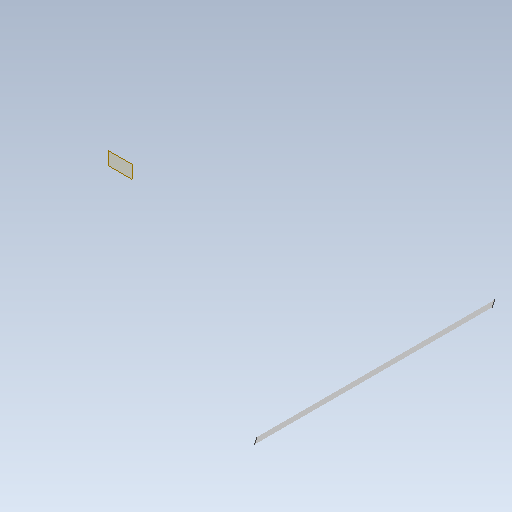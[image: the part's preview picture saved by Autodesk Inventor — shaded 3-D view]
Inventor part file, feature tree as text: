
AUTODESK INVENTOR PART (.ipt)
format: ipt  version: 2021 (Build 250183000, 183)  size: 104,960 bytes
history: native  units: mm
features: other x4, extrude x1, chamfer x1, reference x1
ambient origin geometry x8: Origin, YZ Plane, XZ Plane, XY Plane, X Axis, Y Axis, Z Axis, Center Point
bodies: Body1 (feature_tree)
feature tree (7):
  other  "Bryła1"
  other  "Płaszczyzna konstrukcyjna1"
  extrude  "Wyciągnięcie proste1"  Depth=230.0mm TaperAngle=0.0deg
  chamfer  "Faza1"  Distance=2.0mm Angle=45.0deg
  reference  "Odniesienie1"
  other  "cw12model.iam"
  other  "shaft:1"
